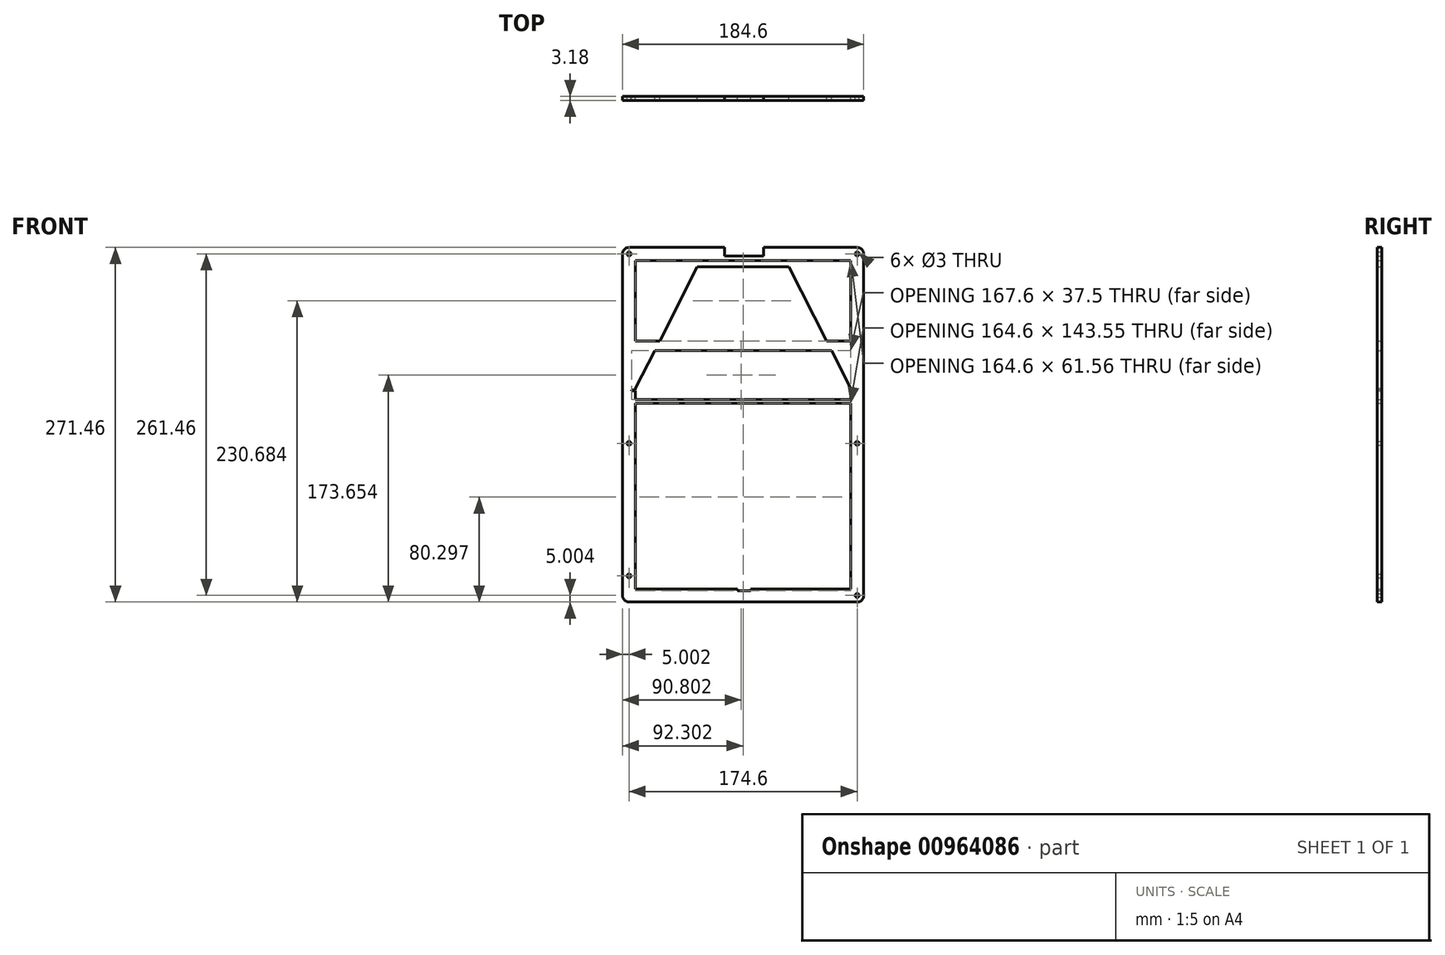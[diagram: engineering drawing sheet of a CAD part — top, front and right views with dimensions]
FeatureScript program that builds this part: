
annotation { "Feature Type Name" : "Feature", "Feature Type Description" : "" }
export const myFeature = defineFeature(function(context is Context, id is Id, definition is map)
    precondition{}
    {
        {
            var Q0;
            Q0=qCreatedBy(makeId("Front.planeOp"),FACE);
            var sketch = newSketch(context, id + "F0", { "sketchPlane" : qUnion([Q0])});
            skLineSegment(sketch, "E0.bottom", {"start": v(-91.77, 132.51) * mm, "end": v(82.83, 132.51) * mm});
            skLineSegment(sketch, "E0.top", {"start": v(-91.77, -138.95) * mm, "end": v(82.83, -138.95) * mm});
            skLineSegment(sketch, "E0.left", {"start": v(-96.77, 127.51) * mm, "end": v(-96.77, -133.95) * mm});
            skLineSegment(sketch, "E0.right", {"start": v(87.83, 127.51) * mm, "end": v(87.83, -133.95) * mm});
            skPoint(sketch, "E1.visualSharp", {"position": v(-96.77, 132.51) * mm});
            skArc(sketch, "E1.filletArc", {"start": v(-91.77, 132.51) * mm, "mid": v(-95.3, 131.05) * mm, "end": v(-96.77, 127.51) * mm});
            skPoint(sketch, "E2.visualSharp", {"position": v(87.83, 132.51) * mm});
            skArc(sketch, "E2.filletArc", {"start": v(87.83, 127.51) * mm, "mid": v(86.37, 131.05) * mm, "end": v(82.83, 132.51) * mm});
            skPoint(sketch, "E3.visualSharp", {"position": v(87.83, -138.95) * mm});
            skArc(sketch, "E3.filletArc", {"start": v(82.83, -138.95) * mm, "mid": v(86.37, -137.48) * mm, "end": v(87.83, -133.95) * mm});
            skPoint(sketch, "E4.visualSharp", {"position": v(-96.77, -138.95) * mm});
            skArc(sketch, "E4.filletArc", {"start": v(-96.77, -133.95) * mm, "mid": v(-95.3, -137.48) * mm, "end": v(-91.77, -138.95) * mm});
            skCircle(sketch, "E5", {"center": v(-91.77, 127.51) * mm, "radius": 1.5 * mm});
            skCircle(sketch, "E6", {"center": v(82.83, 127.51) * mm, "radius": 1.5 * mm});
            skCircle(sketch, "E7", {"center": v(82.83, -133.95) * mm, "radius": 1.5 * mm});
            skCircle(sketch, "E8", {"center": v(-91.77, -17.49) * mm, "radius": 1.5 * mm});
            skCircle(sketch, "E9", {"center": v(82.83, -17.49) * mm, "radius": 1.5 * mm});
            skLineSegment(sketch, "E10.bottom", {"start": v(-86.77, 122.51) * mm, "end": v(77.83, 122.51) * mm});
            skLineSegment(sketch, "E10.top", {"start": v(-86.77, -128.95) * mm, "end": v(77.83, -128.95) * mm});
            skLineSegment(sketch, "E10.left", {"start": v(-86.77, 122.51) * mm, "end": v(-86.77, -128.95) * mm});
            skLineSegment(sketch, "E10.right", {"start": v(77.83, 122.51) * mm, "end": v(77.83, -128.95) * mm});
            skLineSegment(sketch, "E11.bottom", {"start": v(-8.77, -128.95) * mm, "end": v(1.23, -128.95) * mm});
            skLineSegment(sketch, "E11.top", {"start": v(-8.77, -130.43) * mm, "end": v(1.23, -130.43) * mm});
            skLineSegment(sketch, "E11.left", {"start": v(-8.77, -128.95) * mm, "end": v(-8.77, -130.43) * mm});
            skLineSegment(sketch, "E11.right", {"start": v(1.23, -128.95) * mm, "end": v(1.23, -130.43) * mm});
            skLineSegment(sketch, "E12.bottom", {"start": v(-11.27, -130.43) * mm, "end": v(3.73, -130.43) * mm});
            skLineSegment(sketch, "E12.top", {"start": v(-11.27, -132.03) * mm, "end": v(3.73, -132.03) * mm});
            skLineSegment(sketch, "E12.left", {"start": v(-11.27, -130.43) * mm, "end": v(-11.27, -132.03) * mm});
            skLineSegment(sketch, "E12.right", {"start": v(3.73, -130.43) * mm, "end": v(3.73, -132.03) * mm});
            skLineSegment(sketch, "E13.bottom", {"start": v(-89.77, 23.45) * mm, "end": v(80.83, 23.45) * mm});
            skLineSegment(sketch, "E13.top", {"start": v(-89.77, 21.45) * mm, "end": v(80.83, 21.45) * mm});
            skLineSegment(sketch, "E13.left", {"start": v(-89.77, 23.45) * mm, "end": v(-89.77, 21.45) * mm});
            skLineSegment(sketch, "E13.right", {"start": v(80.83, 23.45) * mm, "end": v(80.83, 21.45) * mm});
            skLineSegment(sketch, "E14.bottom", {"start": v(-86.77, 23.45) * mm, "end": v(77.83, 23.45) * mm});
            skLineSegment(sketch, "E14.left", {"start": v(-86.77, 23.45) * mm, "end": v(-86.77, 24.64) * mm});
            skLineSegment(sketch, "E14.right", {"start": v(77.83, 23.45) * mm, "end": v(77.83, 24.64) * mm});
            skLineSegment(sketch, "E15.bottom", {"start": v(77.83, 21.45) * mm, "end": v(-86.77, 21.45) * mm});
            skLineSegment(sketch, "E15.top", {"start": v(77.83, 13.12) * mm, "end": v(-86.77, 13.12) * mm});
            skLineSegment(sketch, "E15.left", {"start": v(77.83, 21.45) * mm, "end": v(77.83, 13.12) * mm});
            skLineSegment(sketch, "E15.right", {"start": v(-86.77, 21.45) * mm, "end": v(-86.77, 13.12) * mm});
            skLineSegment(sketch, "E16.bottom", {"start": v(-39.47, 124.21) * mm, "end": v(30.53, 124.21) * mm});
            skLineSegment(sketch, "E16.top", {"start": v(-39.47, 122.51) * mm, "end": v(30.53, 122.51) * mm});
            skLineSegment(sketch, "E16.left", {"start": v(-39.47, 124.21) * mm, "end": v(-39.47, 122.51) * mm});
            skLineSegment(sketch, "E16.right", {"start": v(30.53, 124.21) * mm, "end": v(30.53, 122.51) * mm});
            skLineSegment(sketch, "E17.bottom", {"start": v(-49.47, 125.81) * mm, "end": v(40.53, 125.81) * mm});
            skLineSegment(sketch, "E17.top", {"start": v(-49.47, 124.21) * mm, "end": v(40.53, 124.21) * mm});
            skLineSegment(sketch, "E17.left", {"start": v(-49.47, 125.81) * mm, "end": v(-49.47, 124.21) * mm});
            skLineSegment(sketch, "E17.right", {"start": v(40.53, 125.81) * mm, "end": v(40.53, 124.21) * mm});
            skLineSegment(sketch, "E18.bottom", {"start": v(-18.77, 132.51) * mm, "end": v(11.23, 132.51) * mm});
            skLineSegment(sketch, "E18.top", {"start": v(-18.77, 125.81) * mm, "end": v(11.23, 125.81) * mm});
            skLineSegment(sketch, "E18.left", {"start": v(-18.77, 132.51) * mm, "end": v(-18.77, 125.81) * mm});
            skLineSegment(sketch, "E18.right", {"start": v(11.23, 132.51) * mm, "end": v(11.23, 125.81) * mm});
            skLineSegment(sketch, "E19.bottom", {"start": v(30.53, 124.21) * mm, "end": v(40.53, 124.21) * mm});
            skLineSegment(sketch, "E19.top", {"start": v(21.23, 125.81) * mm, "end": v(40.53, 125.81) * mm});
            skLineSegment(sketch, "E19.right", {"start": v(40.53, 124.21) * mm, "end": v(40.53, 125.81) * mm});
            skLineSegment(sketch, "E20.bottom", {"start": v(-39.47, 124.21) * mm, "end": v(-49.47, 124.21) * mm});
            skLineSegment(sketch, "E20.top", {"start": v(-28.77, 125.81) * mm, "end": v(-49.47, 125.81) * mm});
            skLineSegment(sketch, "E20.right", {"start": v(-49.47, 124.21) * mm, "end": v(-49.47, 125.81) * mm});
            skLineSegment(sketch, "E21.bottom", {"start": v(30.53, 122.51) * mm, "end": v(40.53, 122.51) * mm});
            skLineSegment(sketch, "E22.bottom", {"start": v(-39.47, 122.51) * mm, "end": v(-40.47, 122.51) * mm});
            skLineSegment(sketch, "E23.top", {"start": v(-86.77, -22.49) * mm, "end": v(-96.77, -22.49) * mm});
            skLineSegment(sketch, "E23.left", {"start": v(-86.77, -130.99) * mm, "end": v(-86.77, -22.49) * mm});
            skLineSegment(sketch, "E23.right", {"start": v(-96.77, -132.28) * mm, "end": v(-96.77, -22.49) * mm});
            skLineSegment(sketch, "E24.top", {"start": v(-39.47, 117.51) * mm, "end": v(30.53, 117.51) * mm});
            skLineSegment(sketch, "E24.left", {"start": v(-39.47, 122.51) * mm, "end": v(-39.47, 117.51) * mm});
            skLineSegment(sketch, "E24.right", {"start": v(30.53, 122.51) * mm, "end": v(30.53, 117.51) * mm});
            skLineSegment(sketch, "E25.bottom", {"start": v(-96.77, -113.95) * mm, "end": v(-86.77, -113.95) * mm});
            skLineSegment(sketch, "E25.top", {"start": v(-96.77, -128.95) * mm, "end": v(-86.77, -128.95) * mm});
            skLineSegment(sketch, "E25.left", {"start": v(-96.77, -113.95) * mm, "end": v(-96.77, -128.95) * mm});
            skLineSegment(sketch, "E25.right", {"start": v(-86.77, -113.95) * mm, "end": v(-86.77, -128.95) * mm});
            skCircle(sketch, "E26", {"center": v(-91.77, -118.95) * mm, "radius": 1.5 * mm});
            skLineSegment(sketch, "E27", {"start": v(-39.47, 117.51) * mm, "end": v(-86.77, 24.64) * mm});
            skLineSegment(sketch, "E28", {"start": v(30.53, 117.51) * mm, "end": v(77.83, 24.64) * mm});
            skLineSegment(sketch, "E29.bottom", {"start": v(-89.77, 23.45) * mm, "end": v(-86.77, 23.45) * mm});
            skLineSegment(sketch, "E29.left", {"start": v(-89.77, 23.45) * mm, "end": v(-89.77, 22.05) * mm});
            skLineSegment(sketch, "E29.right", {"start": v(-86.77, 23.45) * mm, "end": v(-86.77, 22.05) * mm});
            skCircle(sketch, "E30", {"center": v(-63.77, 79.64) * mm, "radius": 1.5 * mm});
            skCircle(sketch, "E31", {"center": v(54.83, 79.64) * mm, "radius": 1.5 * mm});
            skLineSegment(sketch, "E32.top", {"start": v(-86.77, 53.45) * mm, "end": v(77.83, 53.45) * mm});
            skLineSegment(sketch, "E32.left", {"start": v(-86.77, 23.45) * mm, "end": v(-86.77, 53.45) * mm});
            skLineSegment(sketch, "E32.right", {"start": v(77.83, 23.45) * mm, "end": v(77.83, 53.45) * mm});
            skLineSegment(sketch, "E33.bottom", {"start": v(80.83, 21.45) * mm, "end": v(77.83, 21.45) * mm});
            skLineSegment(sketch, "E33.top", {"start": v(80.83, 22.85) * mm, "end": v(77.83, 22.85) * mm});
            skLineSegment(sketch, "E33.left", {"start": v(80.83, 21.45) * mm, "end": v(80.83, 22.85) * mm});
            skLineSegment(sketch, "E33.right", {"start": v(77.83, 21.45) * mm, "end": v(77.83, 22.85) * mm});
            skLineSegment(sketch, "E34.bottom", {"start": v(-89.77, 22.85) * mm, "end": v(-86.77, 22.85) * mm});
            skLineSegment(sketch, "E34.top", {"start": v(-89.77, 21.45) * mm, "end": v(-86.77, 21.45) * mm});
            skLineSegment(sketch, "E34.left", {"start": v(-89.77, 22.85) * mm, "end": v(-89.77, 21.45) * mm});
            skLineSegment(sketch, "E34.right", {"start": v(-86.77, 22.85) * mm, "end": v(-86.77, 21.45) * mm});
            skLineSegment(sketch, "E35.bottom", {"start": v(77.83, 23.45) * mm, "end": v(-86.77, 23.45) * mm});
            skLineSegment(sketch, "E35.top", {"start": v(77.83, 64.1) * mm, "end": v(-86.77, 64.1) * mm});
            skLineSegment(sketch, "E35.left", {"start": v(77.83, 23.45) * mm, "end": v(77.83, 64.1) * mm});
            skLineSegment(sketch, "E35.right", {"start": v(-86.77, 23.45) * mm, "end": v(-86.77, 64.1) * mm});
            skLineSegment(sketch, "E36.bottom", {"start": v(-86.77, 60.95) * mm, "end": v(77.83, 60.95) * mm});
            skLineSegment(sketch, "E36.top", {"start": v(-86.77, 15.95) * mm, "end": v(77.83, 15.95) * mm});
            skLineSegment(sketch, "E36.left", {"start": v(-86.77, 60.95) * mm, "end": v(-86.77, 15.95) * mm});
            skLineSegment(sketch, "E36.right", {"start": v(77.83, 60.95) * mm, "end": v(77.83, 15.95) * mm});
            skSolve(sketch);
        }
        {
            var Q0;
            {var subQ0=sQuery(id+"F0.wireOp",EDGE,"E14.bottom");var subQ5=sQuery(id+"F0.wireOp",EDGE,"YFpRqNfl-pSxB-0mzl-IsoP-hRtGSdPQFIZJ.left");var subQ6=makeQuery(id+"F0.imprint","INTERSECT",VERTEX,{"derivedFrom":[subQ0,subQ5]});Q0=makeQuery(id+"F0.imprint","IMPRINT",FACE,{"disambiguationData":[TD([[makeQuery(id+"F0.imprint","IMPRINT",EDGE,{"disambiguationData":[TD([[subQ6,-1.0]])],"derivedFrom":subQ5}),-1.0]])]});}
            var Q1;
            {var subQ0=sQuery(id+"F0.wireOp",EDGE,"E14.bottom");var subQ5=sQuery(id+"F0.wireOp",EDGE,"YFpRqNfl-pSxB-0mzl-IsoP-hRtGSdPQFIZJ.right");var subQ6=makeQuery(id+"F0.imprint","INTERSECT",VERTEX,{"derivedFrom":[subQ0,subQ5]});Q1=makeQuery(id+"F0.imprint","IMPRINT",FACE,{"disambiguationData":[TD([[makeQuery(id+"F0.imprint","IMPRINT",EDGE,{"disambiguationData":[TD([[subQ6,-1.0]])],"derivedFrom":subQ5}),1.0]])]});}
            var Q2;
            {var subQ5=sQuery(id+"F0.wireOp",EDGE,"E13.right");Q2=makeQuery(id+"F0.imprint","IMPRINT",FACE,{"disambiguationData":[TD([[makeQuery(id+"F0.imprint","IMPRINT",EDGE,{"derivedFrom":subQ5}),-1.0]])]});}
            var Q3;
            {var subQ5=sQuery(id+"F0.wireOp",EDGE,"E13.left");Q3=makeQuery(id+"F0.imprint","IMPRINT",FACE,{"disambiguationData":[TD([[makeQuery(id+"F0.imprint","IMPRINT",EDGE,{"derivedFrom":subQ5}),1.0]])]});}
            var Q4;
            {var subQ9=sQuery(id+"F0.wireOp",EDGE,"E1.filletArc");Q4=makeQuery(id+"F0.imprint","IMPRINT",FACE,{"disambiguationData":[TD([[makeQuery(id+"F0.imprint","IMPRINT",EDGE,{"derivedFrom":subQ9}),1.0]])]});}
            var Q5;
            Q5=makeQuery(id+"F0.imprint","IMPRINT",FACE,{"disambiguationData":[TD([[makeQuery(id+"F0.imprint","IMPRINT",EDGE,{"derivedFrom":sQuery(id+"F0.wireOp",EDGE,"E25.bottom")}),-1.0]])]});
            var Q6;
            {var subQ0=sQuery(id+"F0.wireOp",EDGE,"E22.bottom");Q6=makeQuery(id+"F0.imprint","IMPRINT",FACE,{"disambiguationData":[TD([[makeQuery(id+"F0.imprint","IMPRINT",EDGE,{"derivedFrom":subQ0}),1.0]])]});}
            var Q7;
            {var subQ0=sQuery(id+"F0.wireOp",EDGE,"E21.bottom");Q7=makeQuery(id+"F0.imprint","IMPRINT",FACE,{"disambiguationData":[TD([[makeQuery(id+"F0.imprint","IMPRINT",EDGE,{"derivedFrom":subQ0}),-1.0]])]});}
            var Q8;
            {var subQ0=sQuery(id+"F0.wireOp",EDGE,"E23.bottom");Q8=makeQuery(id+"F0.imprint","IMPRINT",FACE,{"disambiguationData":[TD([[makeQuery(id+"F0.imprint","IMPRINT",EDGE,{"derivedFrom":subQ0}),-1.0]])]});}
            var Q9;
            Q9=makeQuery(id+"F0.imprint","IMPRINT",FACE,{"disambiguationData":[TD([[makeQuery(id+"F0.imprint","IMPRINT",EDGE,{"derivedFrom":sQuery(id+"F0.wireOp",EDGE,"E29.bottom")}),-1.0]])]});
            var Q10;
            {var subQ0=sQuery(id+"F0.wireOp",EDGE,"E32.right");var subQ1=sQuery(id+"F0.wireOp",EDGE,"E28");var subQ2=makeQuery(id+"F0.imprint","INTERSECT",VERTEX,{"derivedFrom":[subQ1,subQ0]});Q10=makeQuery(id+"F0.imprint","IMPRINT",FACE,{"disambiguationData":[TD([[makeQuery(id+"F0.imprint","IMPRINT",EDGE,{"disambiguationData":[TD([[subQ2,1.0]])],"derivedFrom":subQ1}),1.0]])]});}
            var Q11;
            {var subQ0=sQuery(id+"F0.wireOp",EDGE,"E32.left");var subQ1=sQuery(id+"F0.wireOp",EDGE,"E27");var subQ2=makeQuery(id+"F0.imprint","INTERSECT",VERTEX,{"derivedFrom":[subQ1,subQ0]});Q11=makeQuery(id+"F0.imprint","IMPRINT",FACE,{"disambiguationData":[TD([[makeQuery(id+"F0.imprint","IMPRINT",EDGE,{"disambiguationData":[TD([[subQ2,1.0]])],"derivedFrom":subQ1}),-1.0]])]});}
            var Q12;
            {var subQ0=sQuery(id+"F0.wireOp",EDGE,"E36.bottom");var subQ1=sQuery(id+"F0.wireOp",EDGE,"E28");var subQ2=makeQuery(id+"F0.imprint","INTERSECT",VERTEX,{"derivedFrom":[subQ1,subQ0]});Q12=makeQuery(id+"F0.imprint","IMPRINT",FACE,{"disambiguationData":[TD([[makeQuery(id+"F0.imprint","IMPRINT",EDGE,{"disambiguationData":[TD([[subQ2,-1.0]])],"derivedFrom":subQ1}),1.0]])]});}
            var Q13;
            {var subQ5=sQuery(id+"F0.wireOp",EDGE,"E35.left");Q13=makeQuery(id+"F0.imprint","IMPRINT",FACE,{"disambiguationData":[TD([[makeQuery(id+"F0.imprint","IMPRINT",EDGE,{"derivedFrom":subQ5}),1.0]])]});}
            var Q14;
            {var subQ0=sQuery(id+"F0.wireOp",EDGE,"E36.bottom");var subQ1=sQuery(id+"F0.wireOp",EDGE,"E27");var subQ2=makeQuery(id+"F0.imprint","INTERSECT",VERTEX,{"derivedFrom":[subQ1,subQ0]});Q14=makeQuery(id+"F0.imprint","IMPRINT",FACE,{"disambiguationData":[TD([[makeQuery(id+"F0.imprint","IMPRINT",EDGE,{"disambiguationData":[TD([[subQ2,-1.0]])],"derivedFrom":subQ1}),-1.0]])]});}
            var Q15;
            {var subQ5=sQuery(id+"F0.wireOp",EDGE,"E35.right");Q15=makeQuery(id+"F0.imprint","IMPRINT",FACE,{"disambiguationData":[TD([[makeQuery(id+"F0.imprint","IMPRINT",EDGE,{"derivedFrom":subQ5}),-1.0]])]});}
            var Q16;
            {var subQ0=sQuery(id+"F0.wireOp",EDGE,"E23.top");Q16=makeQuery(id+"F0.imprint","IMPRINT",FACE,{"disambiguationData":[TD([[makeQuery(id+"F0.imprint","IMPRINT",EDGE,{"derivedFrom":subQ0}),1.0]])]});}
            var Q17;
            {var subQ7=sQuery(id+"F0.wireOp",EDGE,"E11.bottom");Q17=makeQuery(id+"F0.imprint","IMPRINT",FACE,{"disambiguationData":[TD([[makeQuery(id+"F0.imprint","IMPRINT",EDGE,{"derivedFrom":subQ7}),1.0]])]});}
            var Q18;
            {var subQ0=sQuery(id+"F0.wireOp",EDGE,"E15.bottom");Q18=makeQuery(id+"F0.imprint","IMPRINT",FACE,{"disambiguationData":[TD([[makeQuery(id+"F0.imprint","IMPRINT",EDGE,{"derivedFrom":subQ0}),1.0]])]});}
            var Q19;
            Q19=makeQuery(id+"F0.imprint","IMPRINT",FACE,{"disambiguationData":[TD([[makeQuery(id+"F0.imprint","IMPRINT",EDGE,{"derivedFrom":sQuery(id+"F0.wireOp",EDGE,"E12.top")}),1.0]])]});
            var Q20;
            Q20=makeQuery(id+"F0.imprint","IMPRINT",FACE,{"disambiguationData":[TD([[makeQuery(id+"F0.imprint","IMPRINT",EDGE,{"derivedFrom":sQuery(id+"F0.wireOp",EDGE,"E0.top")}),1.0]])]});
            var Q21;
            Q21=makeQuery(id+"F0.imprint","IMPRINT",FACE,{"disambiguationData":[TD([[makeQuery(id+"F0.imprint","IMPRINT",EDGE,{"derivedFrom":sQuery(id+"F0.wireOp",EDGE,"E11.bottom")}),-1.0]])]});
            var Q22;
            Q22=makeQuery(id+"F0.imprint","IMPRINT",FACE,{"disambiguationData":[TD([[makeQuery(id+"F0.imprint","IMPRINT",EDGE,{"derivedFrom":sQuery(id+"F0.wireOp",EDGE,"E15.top")}),-1.0]])]});
            var Q23;
            {var subQ4=sQuery(id+"F0.wireOp",EDGE,"E15.bottom");Q23=makeQuery(id+"F0.imprint","IMPRINT",FACE,{"disambiguationData":[TD([[makeQuery(id+"F0.imprint","IMPRINT",EDGE,{"derivedFrom":subQ4}),-1.0]])]});}
            var Q24;
            {var subQ0=sQuery(id+"F0.wireOp",EDGE,"E35.bottom");Q24=makeQuery(id+"F0.imprint","IMPRINT",FACE,{"disambiguationData":[TD([[makeQuery(id+"F0.imprint","IMPRINT",EDGE,{"derivedFrom":subQ0}),-1.0]])]});}
            var Q25;
            {var subQ0=sQuery(id+"F0.wireOp",EDGE,"E36.bottom");var subQ1=sQuery(id+"F0.wireOp",EDGE,"E27");var subQ2=makeQuery(id+"F0.imprint","INTERSECT",VERTEX,{"derivedFrom":[subQ1,subQ0]});Q25=makeQuery(id+"F0.imprint","IMPRINT",FACE,{"disambiguationData":[TD([[makeQuery(id+"F0.imprint","IMPRINT",EDGE,{"disambiguationData":[TD([[subQ2,-1.0]])],"derivedFrom":subQ1}),1.0]])]});}
            var Q26;
            {var subQ0=sQuery(id+"F0.wireOp",EDGE,"E35.top");var subQ1=sQuery(id+"F0.wireOp",EDGE,"E27");var subQ2=makeQuery(id+"F0.imprint","INTERSECT",VERTEX,{"derivedFrom":[subQ1,subQ0]});Q26=makeQuery(id+"F0.imprint","IMPRINT",FACE,{"disambiguationData":[TD([[makeQuery(id+"F0.imprint","IMPRINT",EDGE,{"disambiguationData":[TD([[subQ2,-1.0]])],"derivedFrom":subQ1}),1.0]])]});}
            var Q27;
            {var subQ0=sQuery(id+"F0.wireOp",EDGE,"E24.top");Q27=makeQuery(id+"F0.imprint","IMPRINT",FACE,{"disambiguationData":[TD([[makeQuery(id+"F0.imprint","IMPRINT",EDGE,{"derivedFrom":subQ0}),-1.0]])]});}
            var Q28;
            Q28=makeQuery(id+"F0.imprint","IMPRINT",FACE,{"disambiguationData":[TD([[makeQuery(id+"F0.imprint","IMPRINT",EDGE,{"derivedFrom":sQuery(id+"F0.wireOp",EDGE,"E17.top")}),1.0]])]});
            var Q29;
            Q29=makeQuery(id+"F0.imprint","IMPRINT",FACE,{"disambiguationData":[TD([[makeQuery(id+"F0.imprint","IMPRINT",EDGE,{"derivedFrom":sQuery(id+"F0.wireOp",EDGE,"E16.left")}),1.0]])]});
            var Q30;
            Q30=makeQuery(id+"F0.imprint","IMPRINT",FACE,{"disambiguationData":[TD([[makeQuery(id+"F0.imprint","IMPRINT",EDGE,{"derivedFrom":sQuery(id+"F0.wireOp",EDGE,"E16.top")}),-1.0]])]});
            var Q31;
            Q31=makeQuery(id+"F0.imprint","IMPRINT",FACE,{"disambiguationData":[TD([[makeQuery(id+"F0.imprint","IMPRINT",EDGE,{"derivedFrom":sQuery(id+"F0.wireOp",EDGE,"E18.bottom")}),-1.0]])]});
            var Q32;
            {var subQ0=sQuery(id+"F0.wireOp",EDGE,"E33.bottom");Q32=makeQuery(id+"F0.imprint","IMPRINT",FACE,{"disambiguationData":[TD([[makeQuery(id+"F0.imprint","IMPRINT",EDGE,{"derivedFrom":subQ0}),-1.0]])]});}
            var Q33;
            {var subQ3=sQuery(id+"F0.wireOp",EDGE,"E34.bottom");Q33=makeQuery(id+"F0.imprint","IMPRINT",FACE,{"disambiguationData":[TD([[makeQuery(id+"F0.imprint","IMPRINT",EDGE,{"derivedFrom":subQ3}),-1.0]])]});}
            extrude(context, id + "F1", {"entities" : qUnion([Q0, Q1, Q2, Q3, Q4, Q5, Q6, Q7, Q8, Q9, Q10, Q11, Q12, Q13, Q14, Q15, Q16, Q17, Q18, Q19, Q20, Q21, Q22, Q23, Q24, Q25, Q26, Q27, Q28, Q29, Q30, Q31, Q32, Q33]), "depth" : 3.17 * mm, "offsetDistance" : 25 * mm});
        }
    });
